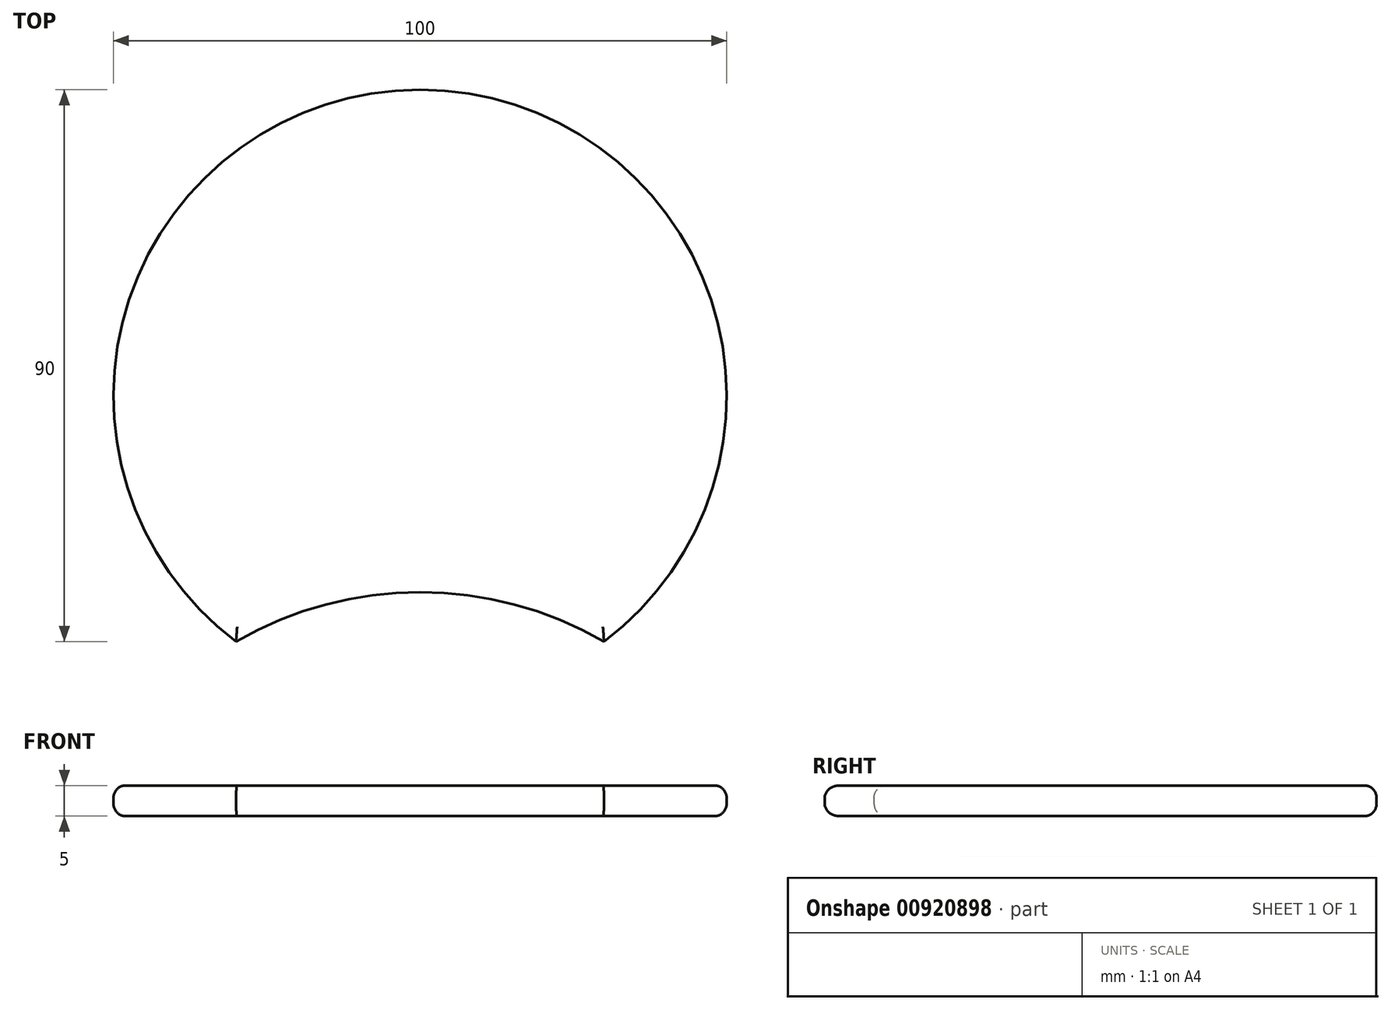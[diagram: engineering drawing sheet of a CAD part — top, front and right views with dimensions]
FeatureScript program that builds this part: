
annotation { "Feature Type Name" : "Feature", "Feature Type Description" : "" }
export const myFeature = defineFeature(function(context is Context, id is Id, definition is map)
    precondition{}
    {
        {
            var Q0;
            Q0=qCreatedBy(makeId("Top.planeOp"),FACE);
            var sketch = newSketch(context, id + "F0", { "sketchPlane" : qUnion([Q0])});
            skArc(sketch, "E0", {"start": v(30, -40) * mm, "mid": v(0, 50) * mm, "end": v(-30, -40) * mm});
            skArc(sketch, "E1", {"start": v(30, -40) * mm, "mid": v(0, -31.96) * mm, "end": v(-30, -40) * mm});
            skSolve(sketch);
        }
        {
            var Q0;
            Q0=makeQuery(id+"F0.imprint","IMPRINT",FACE,{"disambiguationData":[TD([[makeQuery(id+"F0.imprint","IMPRINT",EDGE,{"derivedFrom":sQuery(id+"F0.wireOp",EDGE,"E0")}),1.0]])]});
            extrude(context, id + "F1", {"entities" : qUnion([Q0]), "depth" : 5 * mm, "offsetDistance" : 25 * mm});
        }
        {
            var Q0;
            Q0=makeQuery(id+"F1.opExtrude","CAP_FACE",FACE,{"disambiguationData":[OSD([sQuery(id+"F0.wireOp",EDGE,"E0"),sQuery(id+"F0.wireOp",EDGE,"E1")])],"isStart":false});
            var Q1;
            Q1=makeQuery(id+"F1.opExtrude","CAP_FACE",FACE,{"disambiguationData":[OSD([sQuery(id+"F0.wireOp",EDGE,"E0"),sQuery(id+"F0.wireOp",EDGE,"E1")])],"isStart":true});
            fillet(context, id + "F2", {"entities" : qUnion([Q0, Q1]), "radius" : 2 * mm, "tangentPropagation" : true, "allowEdgeOverflow" : false});
        }
    });
